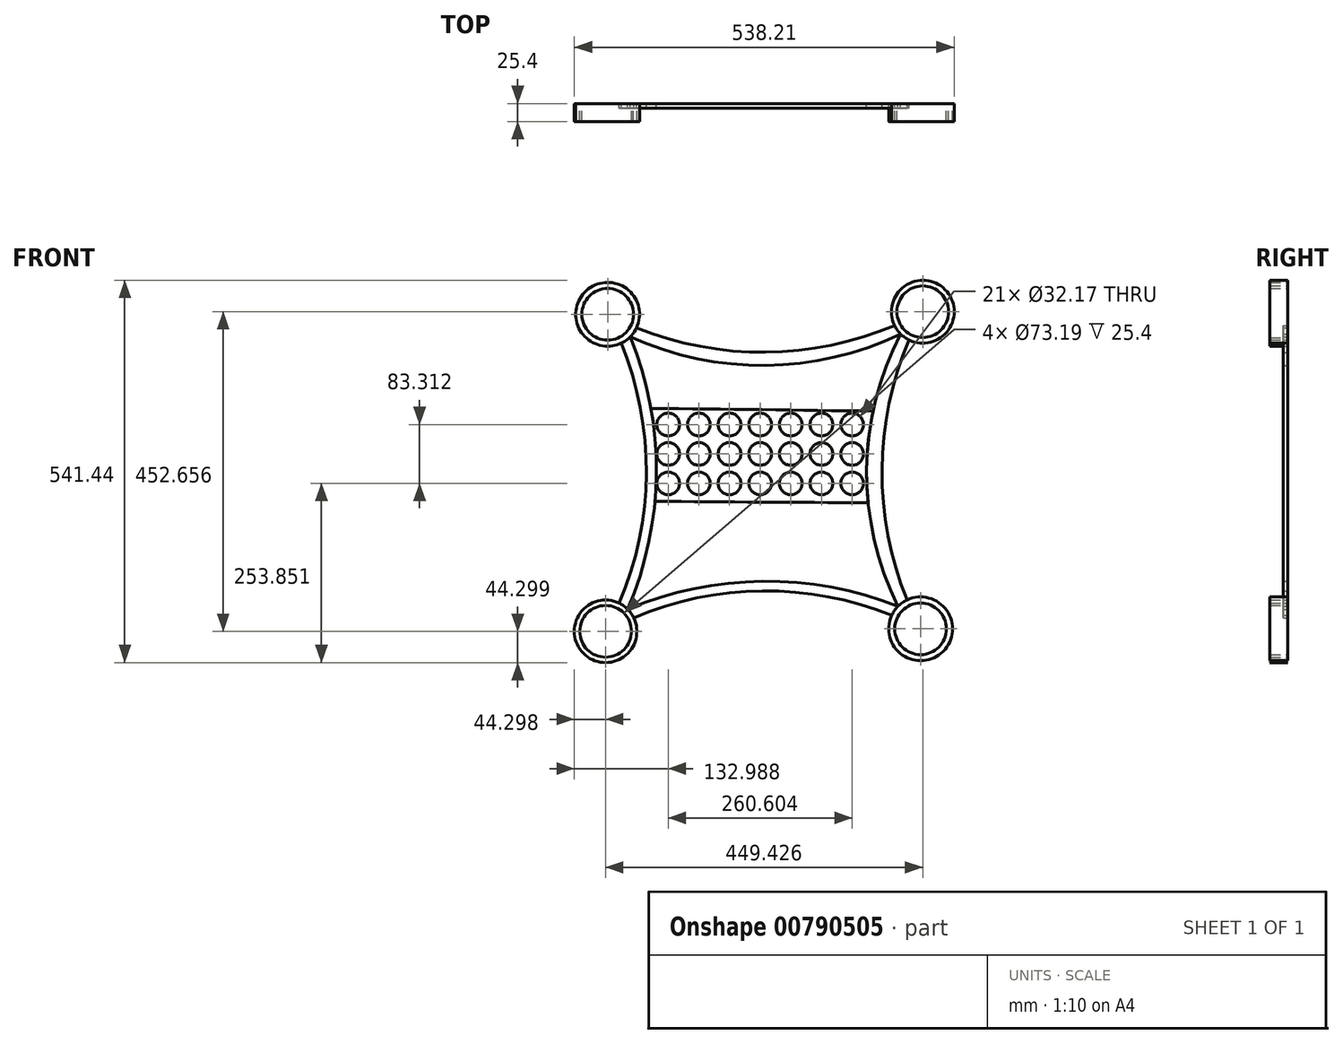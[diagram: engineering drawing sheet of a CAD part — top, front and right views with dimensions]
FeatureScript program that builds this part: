
annotation { "Feature Type Name" : "Feature", "Feature Type Description" : "" }
export const myFeature = defineFeature(function(context is Context, id is Id, definition is map)
    precondition{}
    {
        {
            var Q0;
            Q0=qCreatedBy(makeId("Front.planeOp"),FACE);
            var sketch = newSketch(context, id + "F0", { "sketchPlane" : qUnion([Q0])});
            skArc(sketch, "E0", {"start": v(-176.8, 181.61) * mm, "mid": v(6.22, 146.75) * mm, "end": v(188.6, 184.84) * mm});
            skArc(sketch, "E1", {"start": v(209.28, 164.14) * mm, "mid": v(170.9, -19.63) * mm, "end": v(206.47, -203.97) * mm});
            skArc(sketch, "E2", {"start": v(184.54, -225.97) * mm, "mid": v(1.51, -191.12) * mm, "end": v(-180.87, -229.22) * mm});
            skArc(sketch, "E3", {"start": v(-201.48, -208.6) * mm, "mid": v(-163.11, -24.77) * mm, "end": v(-198.73, 159.61) * mm});
            skCircle(sketch, "E4", {"center": v(-217.82, 200.56) * mm, "radius": 45.18 * mm});
            skCircle(sketch, "E5", {"center": v(228.66, 204.18) * mm, "radius": 44.49 * mm});
            skCircle(sketch, "E6", {"center": v(-220.76, -248.47) * mm, "radius": 44.3 * mm});
            skCircle(sketch, "E7", {"center": v(225.55, -244.9) * mm, "radius": 45.17 * mm});
            skCircle(sketch, "E8", {"center": v(-217.82, 200.56) * mm, "radius": 36.6 * mm});
            skCircle(sketch, "E9", {"center": v(228.66, 204.18) * mm, "radius": 36.6 * mm});
            skCircle(sketch, "E10", {"center": v(-220.76, -248.47) * mm, "radius": 36.6 * mm});
            skCircle(sketch, "E11", {"center": v(225.55, -244.9) * mm, "radius": 36.6 * mm});
            skArc(sketch, "E12", {"start": v(188.6, 184.84) * mm, "mid": v(197.2, 172.75) * mm, "end": v(209.28, 164.14) * mm});
            skArc(sketch, "E13", {"start": v(-198.73, 159.61) * mm, "mid": v(-185.8, 168.64) * mm, "end": v(-176.8, 181.61) * mm});
            skArc(sketch, "E14", {"start": v(-180.87, -229.22) * mm, "mid": v(-189.45, -217.19) * mm, "end": v(-201.48, -208.6) * mm});
            skArc(sketch, "E15", {"start": v(206.47, -203.97) * mm, "mid": v(193.56, -213.03) * mm, "end": v(184.54, -225.97) * mm});
            skArc(sketch, "E16", {"start": v(-189.45, -217.19) * mm, "mid": v(-148.9, -24.64) * mm, "end": v(-185.8, 168.64) * mm});
            skCircle(sketch, "E17", {"center": v(-132.07, 44.4) * mm, "radius": 16.09 * mm});
            skCircle(sketch, "E18.0.1.0", {"center": v(-132.07, 2.74) * mm, "radius": 16.09 * mm});
            skCircle(sketch, "E18.0.2.0", {"center": v(-132.07, -38.92) * mm, "radius": 16.09 * mm});
            skCircle(sketch, "E18.1.0.0", {"center": v(-88.64, 44.4) * mm, "radius": 16.09 * mm});
            skCircle(sketch, "E18.1.1.0", {"center": v(-88.64, 2.74) * mm, "radius": 16.09 * mm});
            skCircle(sketch, "E18.1.2.0", {"center": v(-88.64, -38.92) * mm, "radius": 16.09 * mm});
            skCircle(sketch, "E18.2.0.0", {"center": v(-45.2, 44.4) * mm, "radius": 16.09 * mm});
            skCircle(sketch, "E18.2.1.0", {"center": v(-45.2, 2.74) * mm, "radius": 16.09 * mm});
            skCircle(sketch, "E18.2.2.0", {"center": v(-45.2, -38.92) * mm, "radius": 16.09 * mm});
            skCircle(sketch, "E18.3.0.0", {"center": v(-1.77, 44.4) * mm, "radius": 16.09 * mm});
            skCircle(sketch, "E18.3.1.0", {"center": v(-1.77, 2.74) * mm, "radius": 16.09 * mm});
            skCircle(sketch, "E18.3.2.0", {"center": v(-1.77, -38.92) * mm, "radius": 16.09 * mm});
            skCircle(sketch, "E18.4.0.0", {"center": v(41.66, 44.4) * mm, "radius": 16.09 * mm});
            skCircle(sketch, "E18.4.1.0", {"center": v(41.66, 2.74) * mm, "radius": 16.09 * mm});
            skCircle(sketch, "E18.4.2.0", {"center": v(41.66, -38.92) * mm, "radius": 16.09 * mm});
            skCircle(sketch, "E18.5.0.0", {"center": v(85.1, 44.4) * mm, "radius": 16.09 * mm});
            skCircle(sketch, "E18.5.1.0", {"center": v(85.1, 2.74) * mm, "radius": 16.09 * mm});
            skCircle(sketch, "E18.5.2.0", {"center": v(85.1, -38.92) * mm, "radius": 16.09 * mm});
            skCircle(sketch, "E18.6.0.0", {"center": v(128.53, 44.4) * mm, "radius": 16.09 * mm});
            skCircle(sketch, "E18.6.1.0", {"center": v(128.53, 2.74) * mm, "radius": 16.09 * mm});
            skCircle(sketch, "E18.6.2.0", {"center": v(128.53, -38.92) * mm, "radius": 16.09 * mm});
            skLineSegment(sketch, "E18.direction1", {"start": v(-132.07, 44.4) * mm, "end": v(-88.64, 44.4) * mm, "construction": true});
            skLineSegment(sketch, "E18.direction2", {"start": v(-132.07, 44.4) * mm, "end": v(-132.07, 2.74) * mm, "construction": true});
            skArc(sketch, "E19", {"start": v(-185.8, 168.64) * mm, "mid": v(6.15, 128.2) * mm, "end": v(197.19, 172.74) * mm});
            skArc(sketch, "E20", {"start": v(197.19, 172.74) * mm, "mid": v(149.07, -19.7) * mm, "end": v(193.56, -213.03) * mm});
            skArc(sketch, "E21", {"start": v(193.56, -213.03) * mm, "mid": v(1.65, -177.56) * mm, "end": v(-189.45, -217.19) * mm});
            skArc(sketch, "E22", {"start": v(158.05, 63.29) * mm, "mid": v(0.76, 65.53) * mm, "end": v(-156.54, 67.25) * mm});
            skArc(sketch, "E23", {"start": v(-150.87, -64.42) * mm, "mid": v(0.17, -65.5) * mm, "end": v(151.2, -66.4) * mm});
            skSolve(sketch);
        }
        {
            var Q0;
            {var subQ0=sQuery(id+"F0.wireOp",EDGE,"E0");Q0=makeQuery(id+"F0.imprint","IMPRINT",FACE,{"disambiguationData":[TD([[makeQuery(id+"F0.imprint","IMPRINT",EDGE,{"derivedFrom":subQ0}),-1.0]])]});}
            var Q1;
            {var subQ0=sQuery(id+"F0.wireOp",EDGE,"E2");Q1=makeQuery(id+"F0.imprint","IMPRINT",FACE,{"disambiguationData":[TD([[makeQuery(id+"F0.imprint","IMPRINT",EDGE,{"derivedFrom":subQ0}),-1.0]])]});}
            var Q2;
            {var subQ0=sQuery(id+"F0.wireOp",EDGE,"E13");var subQ1=sQuery(id+"F0.wireOp",EDGE,"E4");var subQ2=makeQuery(id+"F0.imprint","INTERSECT",VERTEX,{"derivedFrom":[sQuery(id+"F0.wireOp",EDGE,"E0"),subQ1,subQ0]});Q2=makeQuery(id+"F0.imprint","IMPRINT",FACE,{"disambiguationData":[TD([[makeQuery(id+"F0.imprint","IMPRINT",EDGE,{"disambiguationData":[TD([[subQ2,1.0]])],"derivedFrom":subQ1}),-1.0]])]});}
            var Q3;
            {var subQ0=sQuery(id+"F0.wireOp",EDGE,"E12");Q3=makeQuery(id+"F0.imprint","IMPRINT",FACE,{"disambiguationData":[TD([[makeQuery(id+"F0.imprint","IMPRINT",EDGE,{"derivedFrom":subQ0}),-1.0]])]});}
            var Q4;
            {var subQ1=sQuery(id+"F0.wireOp",EDGE,"E6");var subQ3=sQuery(id+"F0.wireOp",EDGE,"E21");var subQ4=makeQuery(id+"F0.imprint","INTERSECT",VERTEX,{"derivedFrom":[subQ1,subQ3]});Q4=makeQuery(id+"F0.imprint","IMPRINT",FACE,{"disambiguationData":[TD([[makeQuery(id+"F0.imprint","IMPRINT",EDGE,{"disambiguationData":[TD([[subQ4,1.0]])],"derivedFrom":subQ1}),1.0]])]});}
            var Q5;
            {var subQ1=sQuery(id+"F0.wireOp",EDGE,"E6");var subQ3=sQuery(id+"F0.wireOp",EDGE,"E16");var subQ4=makeQuery(id+"F0.imprint","INTERSECT",VERTEX,{"derivedFrom":[subQ1,subQ3]});Q5=makeQuery(id+"F0.imprint","IMPRINT",FACE,{"disambiguationData":[TD([[makeQuery(id+"F0.imprint","IMPRINT",EDGE,{"disambiguationData":[TD([[subQ4,-1.0]])],"derivedFrom":subQ1}),1.0]])]});}
            var Q6;
            {var subQ1=sQuery(id+"F0.wireOp",EDGE,"E7");var subQ3=sQuery(id+"F0.wireOp",EDGE,"E20");var subQ4=makeQuery(id+"F0.imprint","INTERSECT",VERTEX,{"derivedFrom":[subQ1,subQ3]});Q6=makeQuery(id+"F0.imprint","IMPRINT",FACE,{"disambiguationData":[TD([[makeQuery(id+"F0.imprint","IMPRINT",EDGE,{"disambiguationData":[TD([[subQ4,1.0]])],"derivedFrom":subQ1}),1.0]])]});}
            var Q7;
            {var subQ1=sQuery(id+"F0.wireOp",EDGE,"E7");var subQ3=sQuery(id+"F0.wireOp",EDGE,"E21");var subQ4=makeQuery(id+"F0.imprint","INTERSECT",VERTEX,{"derivedFrom":[subQ1,subQ3]});Q7=makeQuery(id+"F0.imprint","IMPRINT",FACE,{"disambiguationData":[TD([[makeQuery(id+"F0.imprint","IMPRINT",EDGE,{"disambiguationData":[TD([[subQ4,-1.0]])],"derivedFrom":subQ1}),1.0]])]});}
            var Q8;
            {var subQ5=sQuery(id+"F0.wireOp",EDGE,"E1");Q8=makeQuery(id+"F0.imprint","IMPRINT",FACE,{"disambiguationData":[TD([[makeQuery(id+"F0.imprint","IMPRINT",EDGE,{"derivedFrom":subQ5}),-1.0]])]});}
            var Q9;
            {var subQ5=sQuery(id+"F0.wireOp",EDGE,"E3");Q9=makeQuery(id+"F0.imprint","IMPRINT",FACE,{"disambiguationData":[TD([[makeQuery(id+"F0.imprint","IMPRINT",EDGE,{"derivedFrom":subQ5}),-1.0]])]});}
            var Q10;
            Q10=makeQuery(id+"F0.imprint","IMPRINT",FACE,{"disambiguationData":[TD([[makeQuery(id+"F0.imprint","IMPRINT",EDGE,{"derivedFrom":sQuery(id+"F0.wireOp",EDGE,"E8")}),-1.0]])]});
            var Q11;
            Q11=makeQuery(id+"F0.imprint","IMPRINT",FACE,{"disambiguationData":[TD([[makeQuery(id+"F0.imprint","IMPRINT",EDGE,{"derivedFrom":sQuery(id+"F0.wireOp",EDGE,"E9")}),-1.0]])]});
            var Q12;
            Q12=makeQuery(id+"F0.imprint","IMPRINT",FACE,{"disambiguationData":[TD([[makeQuery(id+"F0.imprint","IMPRINT",EDGE,{"derivedFrom":sQuery(id+"F0.wireOp",EDGE,"E11")}),-1.0]])]});
            var Q13;
            Q13=makeQuery(id+"F0.imprint","IMPRINT",FACE,{"disambiguationData":[TD([[makeQuery(id+"F0.imprint","IMPRINT",EDGE,{"derivedFrom":sQuery(id+"F0.wireOp",EDGE,"E10")}),-1.0]])]});
            extrude(context, id + "F1", {"entities" : qUnion([Q0, Q1, Q2, Q3, Q4, Q5, Q6, Q7, Q8, Q9, Q10, Q11, Q12, Q13]), "depth" : 6.35 * mm, "offsetDistance" : 25.4 * mm});
        }
        {
            var Q0;
            Q0=makeQuery(id+"F0.imprint","IMPRINT",FACE,{"disambiguationData":[TD([[makeQuery(id+"F0.imprint","IMPRINT",EDGE,{"derivedFrom":sQuery(id+"F0.wireOp",EDGE,"E10")}),-1.0]])]});
            var Q1;
            Q1=makeQuery(id+"F0.imprint","IMPRINT",FACE,{"disambiguationData":[TD([[makeQuery(id+"F0.imprint","IMPRINT",EDGE,{"derivedFrom":sQuery(id+"F0.wireOp",EDGE,"E11")}),-1.0]])]});
            var Q2;
            Q2=makeQuery(id+"F0.imprint","IMPRINT",FACE,{"disambiguationData":[TD([[makeQuery(id+"F0.imprint","IMPRINT",EDGE,{"derivedFrom":sQuery(id+"F0.wireOp",EDGE,"E9")}),-1.0]])]});
            var Q3;
            Q3=makeQuery(id+"F0.imprint","IMPRINT",FACE,{"disambiguationData":[TD([[makeQuery(id+"F0.imprint","IMPRINT",EDGE,{"derivedFrom":sQuery(id+"F0.wireOp",EDGE,"E8")}),-1.0]])]});
            extrude(context, id + "F2", {"entities" : qUnion([Q0, Q1, Q2, Q3]), "operationType" : NewBodyOperationType.ADD, "depth" : 25.4 * mm, "offsetDistance" : 25.4 * mm});
        }
        {
            var Q0;
            Q0=makeQuery(id+"F0.imprint","IMPRINT",FACE,{"disambiguationData":[TD([[makeQuery(id+"F0.imprint","IMPRINT",EDGE,{"derivedFrom":sQuery(id+"F0.wireOp",EDGE,"E18.3.1.0")}),1.0]])]});
            var sketch = newSketch(context, id + "F3", { "sketchPlane" : qUnion([Q0])});
            skSolve(sketch);
        }
        {
            var Q0;
            Q0 = qSketchRegion(id + "F3", true);
            var Q1;
            Q1=makeQuery(id+"F0.imprint","IMPRINT",FACE,{"disambiguationData":[TD([[makeQuery(id+"F0.imprint","IMPRINT",EDGE,{"derivedFrom":sQuery(id+"F0.wireOp",EDGE,"E17")}),-1.0]])]});
            extrude(context, id + "F4", {"entities" : qUnion([Q0, Q1]), "operationType" : NewBodyOperationType.ADD, "depth" : 0.76 * mm, "offsetDistance" : 25.4 * mm});
        }
    });
